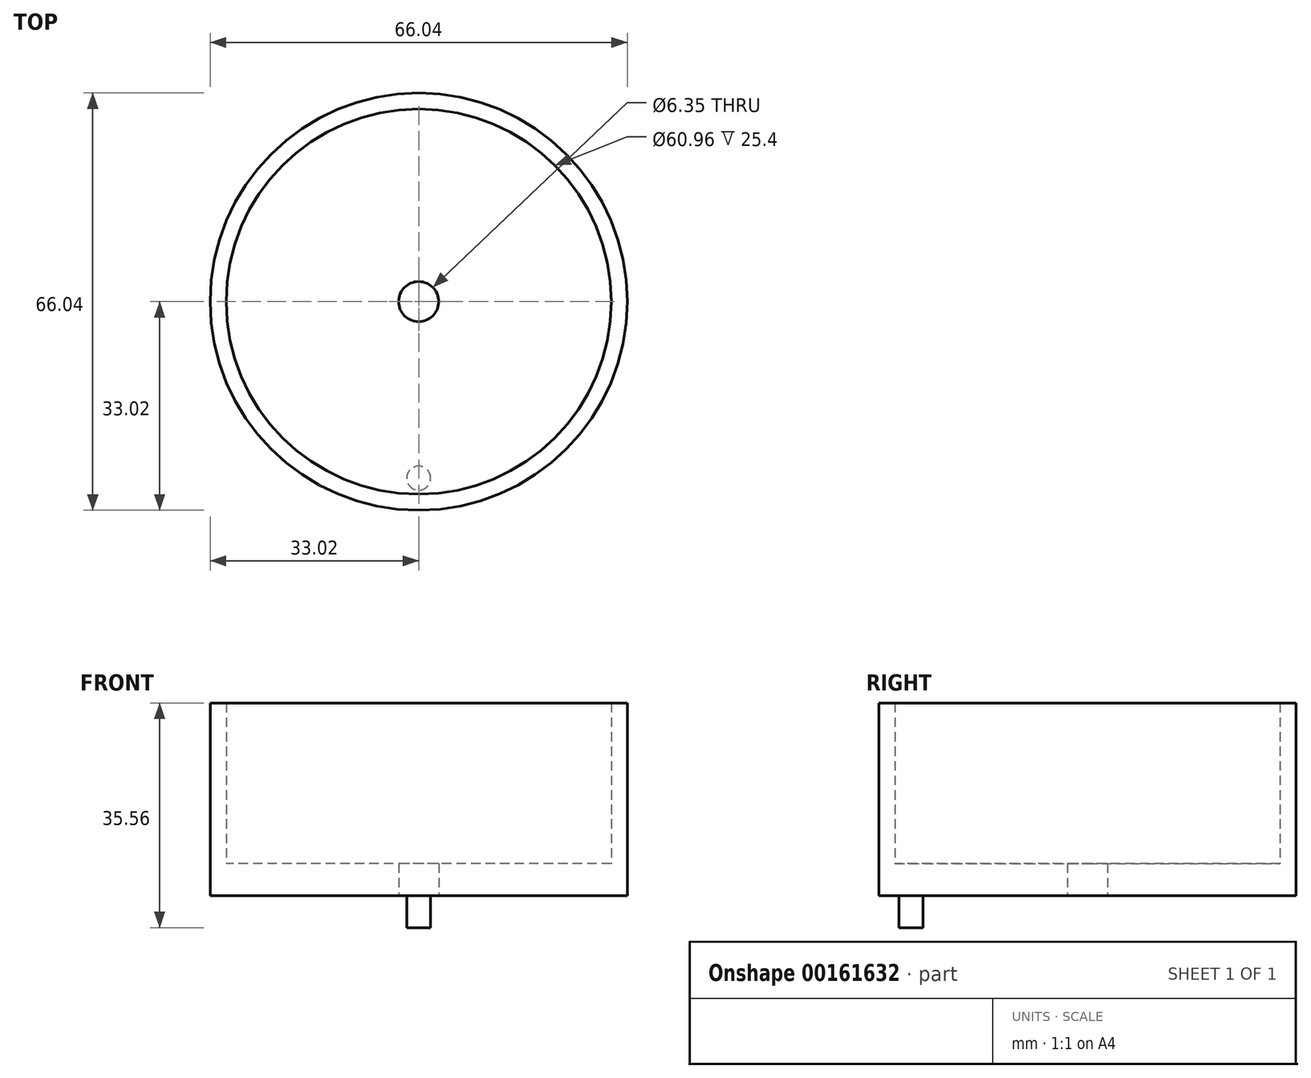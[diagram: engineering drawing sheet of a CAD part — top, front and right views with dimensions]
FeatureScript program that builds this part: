
annotation { "Feature Type Name" : "Feature", "Feature Type Description" : "" }
export const myFeature = defineFeature(function(context is Context, id is Id, definition is map)
    precondition{}
    {
        {
            var Q0;
            Q0=qCreatedBy(makeId("Top.planeOp"),FACE);
            var sketch = newSketch(context, id + "F0", { "sketchPlane" : qUnion([Q0])});
            skCircle(sketch, "E0", {"center": v(0, 0) * mm, "radius": 33.02 * mm});
            skCircle(sketch, "E1", {"center": v(0, 0) * mm, "radius": 3.18 * mm});
            skSolve(sketch);
        }
        {
            var Q0;
            Q0=makeQuery(id+"F0.imprint","IMPRINT",FACE,{"disambiguationData":[TD([[makeQuery(id+"F0.imprint","IMPRINT",EDGE,{"derivedFrom":sQuery(id+"F0.wireOp",EDGE,"E0")}),1.0]])]});
            extrude(context, id + "F1", {"entities" : qUnion([Q0]), "depth" : 5.08 * mm});
        }
        {
            var Q0;
            Q0=makeQuery(id+"F1.opExtrude","CAP_FACE",FACE,{"disambiguationData":[OSD([sQuery(id+"F0.wireOp",EDGE,"E0"),sQuery(id+"F0.wireOp",EDGE,"E1")])],"isStart":false});
            var sketch = newSketch(context, id + "F2", { "sketchPlane" : qUnion([Q0])});
            skCircle(sketch, "E2", {"center": v(0, 0) * mm, "radius": 30.48 * mm});
            skSolve(sketch);
        }
        {
            var Q0;
            Q0=makeQuery(id+"F2.imprint","IMPRINT",FACE,{"disambiguationData":[TD([[makeQuery(id+"F2.imprint","IMPRINT",EDGE,{"derivedFrom":sQuery(id+"F2.wireOp",EDGE,"E2")}),-1.0]])]});
            extrude(context, id + "F3", {"entities" : qUnion([Q0]), "operationType" : NewBodyOperationType.ADD, "depth" : 25.4 * mm});
        }
        {
            var Q0;
            Q0=makeQuery(id+"F1.opExtrude","CAP_FACE",FACE,{"disambiguationData":[OSD([sQuery(id+"F0.wireOp",EDGE,"E0"),sQuery(id+"F0.wireOp",EDGE,"E1")])],"isStart":true});
            var sketch = newSketch(context, id + "F4", { "sketchPlane" : qUnion([Q0])});
            skLineSegment(sketch, "E3", {"start": v(0, 0) * mm, "end": v(0, 33.02) * mm});
            skPoint(sketch, "E4", {"position": v(0, 27.94) * mm});
            skCircle(sketch, "E5", {"center": v(0, 27.94) * mm, "radius": 1.9 * mm});
            skSolve(sketch);
        }
        {
            var Q0;
            {var subQ0=sQuery(id+"F4.wireOp",EDGE,"E5");var subQ1=sQuery(id+"F4.wireOp",EDGE,"E3");var subQ2=makeQuery(id+"F4.imprint","INTERSECT",VERTEX,{"disambiguationData":[OD(0.0)],"derivedFrom":[subQ1,subQ0]});Q0=makeQuery(id+"F4.imprint","IMPRINT",FACE,{"disambiguationData":[TD([[makeQuery(id+"F4.imprint","IMPRINT",EDGE,{"disambiguationData":[TD([[subQ2,1.0]])],"derivedFrom":subQ1}),-1.0]])]});}
            var Q1;
            {var subQ0=sQuery(id+"F4.wireOp",EDGE,"E5");var subQ1=sQuery(id+"F4.wireOp",EDGE,"E3");var subQ2=makeQuery(id+"F4.imprint","INTERSECT",VERTEX,{"disambiguationData":[OD(0.0)],"derivedFrom":[subQ1,subQ0]});Q1=makeQuery(id+"F4.imprint","IMPRINT",FACE,{"disambiguationData":[TD([[makeQuery(id+"F4.imprint","IMPRINT",EDGE,{"disambiguationData":[TD([[subQ2,1.0]])],"derivedFrom":subQ1}),1.0]])]});}
            extrude(context, id + "F5", {"entities" : qUnion([Q0, Q1]), "operationType" : NewBodyOperationType.ADD, "depth" : 5.08 * mm});
        }
    });
